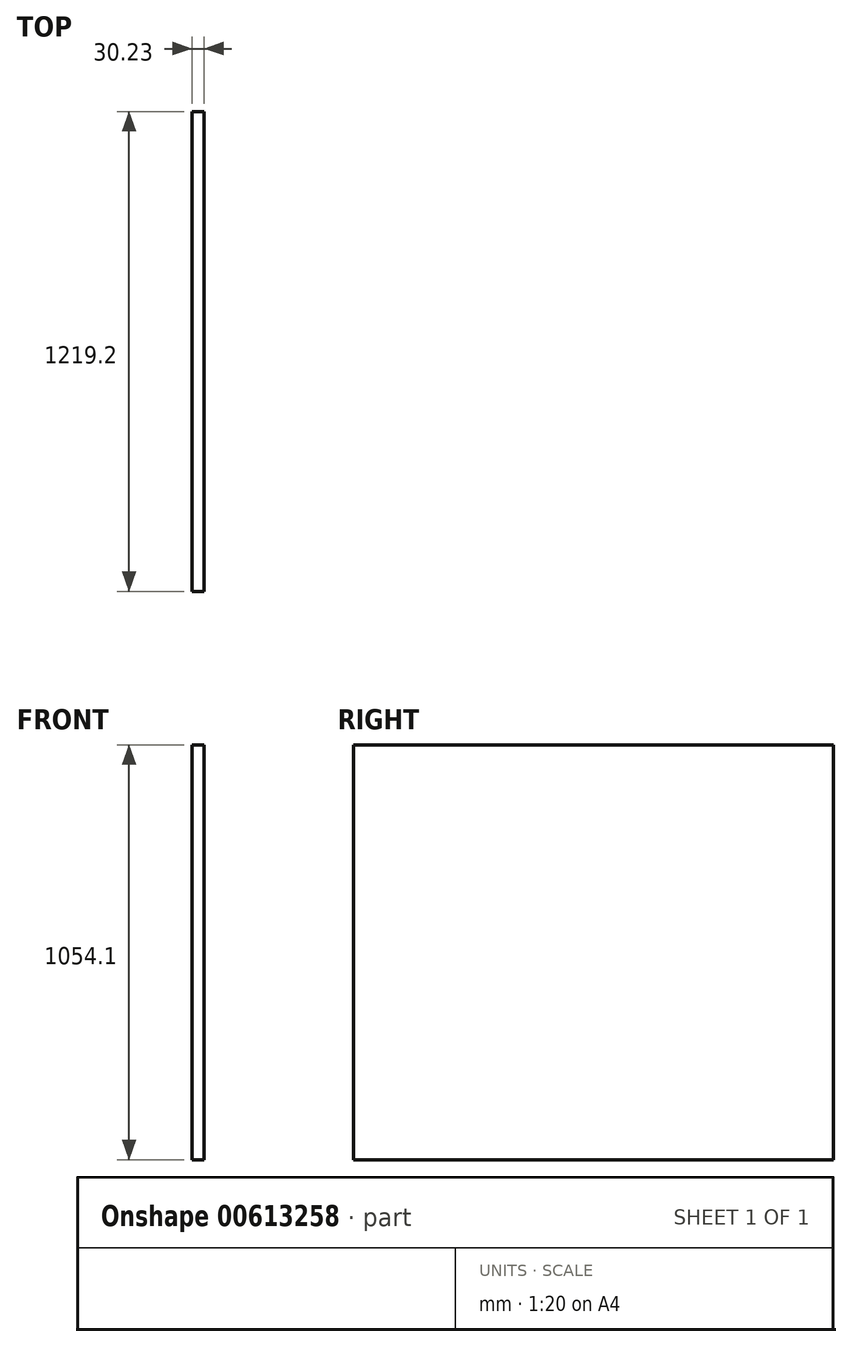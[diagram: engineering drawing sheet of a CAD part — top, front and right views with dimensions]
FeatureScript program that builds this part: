
annotation { "Feature Type Name" : "Feature", "Feature Type Description" : "" }
export const myFeature = defineFeature(function(context is Context, id is Id, definition is map)
    precondition{}
    {
        {
            var Q0;
            Q0=qCreatedBy(makeId("Right.planeOp"),FACE);
            var sketch = newSketch(context, id + "F0", { "sketchPlane" : qUnion([Q0])});
            skLineSegment(sketch, "E0.bottom", {"start": v(609.6, 527.05) * mm, "end": v(-609.6, 527.05) * mm});
            skLineSegment(sketch, "E0.top", {"start": v(609.6, -527.05) * mm, "end": v(-609.6, -527.05) * mm});
            skLineSegment(sketch, "E0.left", {"start": v(609.6, 527.05) * mm, "end": v(609.6, -527.05) * mm});
            skLineSegment(sketch, "E0.right", {"start": v(-609.6, 527.05) * mm, "end": v(-609.6, -527.05) * mm});
            skPoint(sketch, "E0.middle", {"position": v(0, 0) * mm});
            skSolve(sketch);
        }
        {
            var Q0;
            Q0=makeQuery(id+"F0.imprint","IMPRINT",FACE,{"disambiguationData":[TD([[makeQuery(id+"F0.imprint","IMPRINT",EDGE,{"derivedFrom":sQuery(id+"F0.wireOp",EDGE,"E0.bottom")}),1.0]])]});
            extrude(context, id + "F1", {"entities" : qUnion([Q0]), "depth" : 30.23 * mm, "offsetDistance" : 25.4 * mm});
        }
    });
